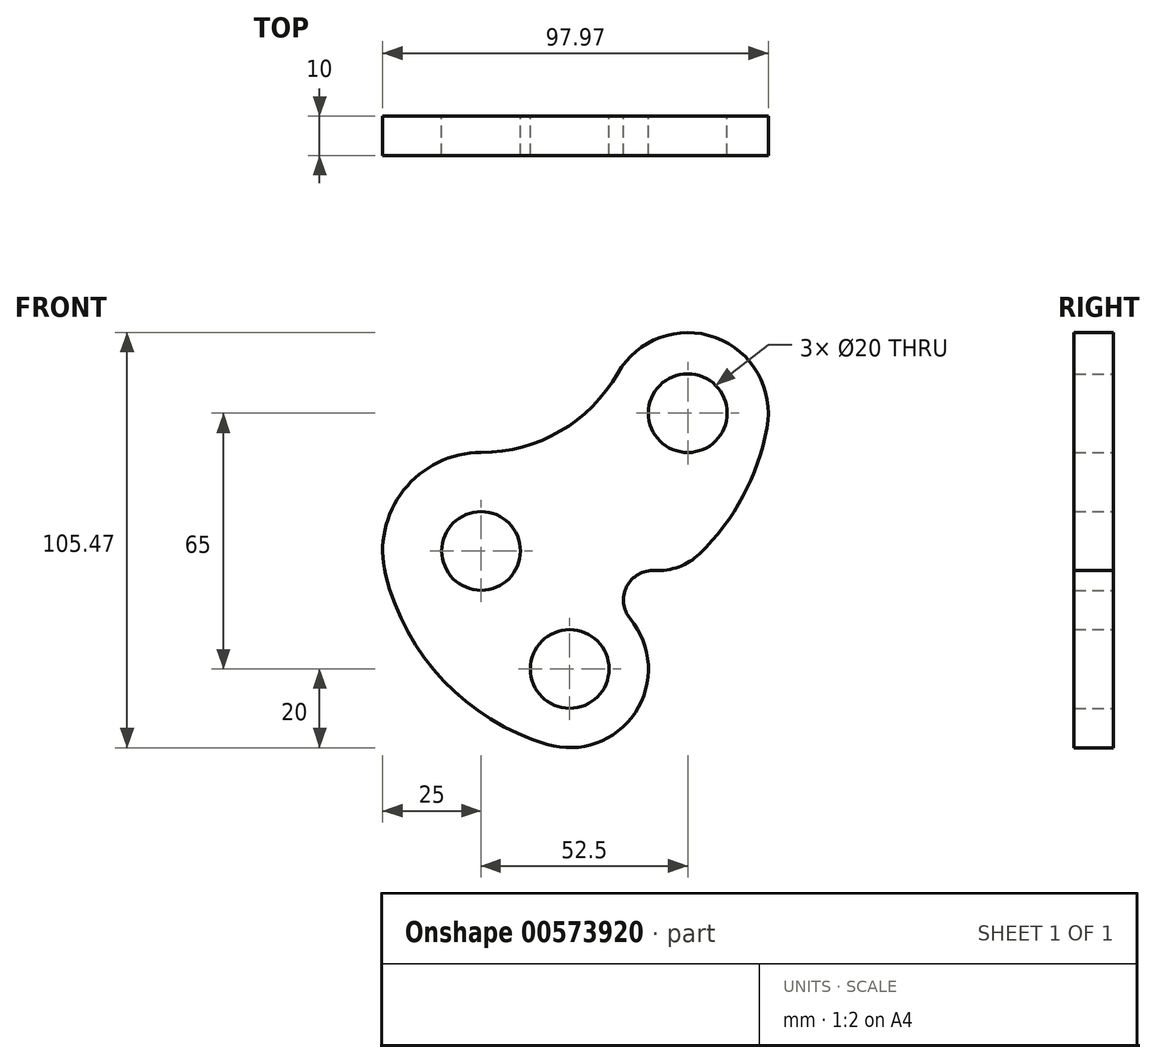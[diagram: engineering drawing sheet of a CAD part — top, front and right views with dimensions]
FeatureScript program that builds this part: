
annotation { "Feature Type Name" : "Feature", "Feature Type Description" : "" }
export const myFeature = defineFeature(function(context is Context, id is Id, definition is map)
    precondition{}
    {
        {
            var Q0;
            Q0=qCreatedBy(makeId("Front.planeOp"),FACE);
            var sketch = newSketch(context, id + "F0", { "sketchPlane" : qUnion([Q0])});
            skArc(sketch, "E0", {"start": v(-24.28, -5.94) * mm, "mid": v(-9.51, -33) * mm, "end": v(16.75, -49.16) * mm});
            skArc(sketch, "E1", {"start": v(0, 25) * mm, "mid": v(-19.66, 15.44) * mm, "end": v(-24.28, -5.94) * mm});
            skCircle(sketch, "E2", {"center": v(0, 0) * mm, "radius": 10 * mm});
            skArc(sketch, "E3", {"start": v(16.75, -49.16) * mm, "mid": v(39.17, -41.05) * mm, "end": v(37.9, -17.24) * mm});
            skArc(sketch, "E4", {"start": v(44.12, -4.97) * mm, "mid": v(37, -9.07) * mm, "end": v(37.9, -17.24) * mm});
            skArc(sketch, "E5", {"start": v(44.12, -4.97) * mm, "mid": v(50.23, -4.06) * mm, "end": v(55.45, -0.76) * mm});
            skArc(sketch, "E6", {"start": v(55.45, -0.76) * mm, "mid": v(66.51, 13.9) * mm, "end": v(72.62, 31.23) * mm});
            skArc(sketch, "E7", {"start": v(72.62, 31.23) * mm, "mid": v(59.56, 54.21) * mm, "end": v(34.73, 45.15) * mm});
            skArc(sketch, "E8", {"start": v(0, 25) * mm, "mid": v(20.08, 30.4) * mm, "end": v(34.73, 45.15) * mm});
            skCircle(sketch, "E9", {"center": v(52.5, 35) * mm, "radius": 10 * mm});
            skCircle(sketch, "E10", {"center": v(22.5, -30) * mm, "radius": 10 * mm});
            skSolve(sketch);
        }
        {
            var Q0;
            Q0 = qSketchRegion(id + "F0", true);
            extrude(context, id + "F1", {"entities" : qUnion([Q0]), "depth" : 10 * mm, "offsetDistance" : 25 * mm});
        }
    });
